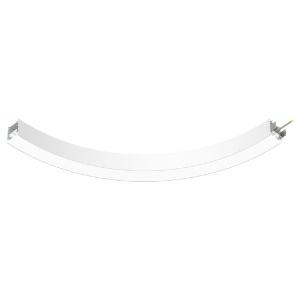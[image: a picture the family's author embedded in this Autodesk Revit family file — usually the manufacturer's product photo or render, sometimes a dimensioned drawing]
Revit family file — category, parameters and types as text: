
# Revit family: super-g_slim_super_g_slim_1550_90deg_hl_ps_led__24w_3160lm_3000k_cri_80_430-1680_5e8c
name_source: partatom
category: Leuchten
revit_build: Autodesk Revit 2016 (Build: 20190508_0715(x64)
units: mm (PartAtom-declared; Revit-internal decimal feet)

## family parameters
Basisbauteil = Fläche
Beim Laden mit Abzugskörper schneiden = Nein
Bemaßung runder Anschluss = Durchmesser verwenden
Gemeinsam genutzt = Nein
Lichtquelle = Nein
Raumberechnungspunkt = Nein
Teiletyp = Normal

## types (1)
- 430-1680-D01 (1 x LED, 480 lm, 3000K)
    Approval mark = CE
    Beschreibung = The insert consists of aluminum-extruded profile. Charming SOFT-EDGE design ensure unparalleled styling. The ballast is integrated and allows for an operation with 220-240V (50/60Hz). SUPER-G SLIM (# 430-1680) ist not dimmable (on/off).
    CIE Flux Codes = 48 79 96 100 71
    Color Rendering = 1B/80…89
    Color Temperature = 3000K
    Height = 90 mm
    Hersteller = Prolicht
    Lamp Light Flux = 480 lm
    Lamp count = 1
    Lampe = 1 x LED
    Length = 146 mm
    Luminous efficacy = 103 lm/W
    ModVariant = Nein
    Modell = 430-1680
    Mounting Place = Ceiling
    Mounting Type = Pendant
    Number of Poles = 1
    OnlyDefault = Ja
    Power Factor = 1
    Product Name = SUPER-G SLIM__SUPER G SLIM 1550/90° HL PS LED: 24W 3160lm 3000K CRI:80
    Product group = Suspended profile systems
    ProductGroupID = 944
    Protection Class = Protection class I
    Protection Degree = IP 20
    RLX_Detail_Level = 1
    RlxData = <blob elided: 38349 chars, md5=fb990a43>
    Scheinlast = 26 VA
    Socket = socket
    Standby Power = 0 W
    System Light Flux = 2723 lm
    System Power = 26 W
    Typenbild = 430-1680.jpg
    URL = http://relux.com
    VarID = 430-1680-d01
    Voltage = 0 V
    Vorgabe-Ansicht = 1800 mm
    Weight = 0.00 kg
    Width = 65 mm

## geometry (parser evidence)
native form markers: Sweep x30
no freeform markers — native parametric forms only
